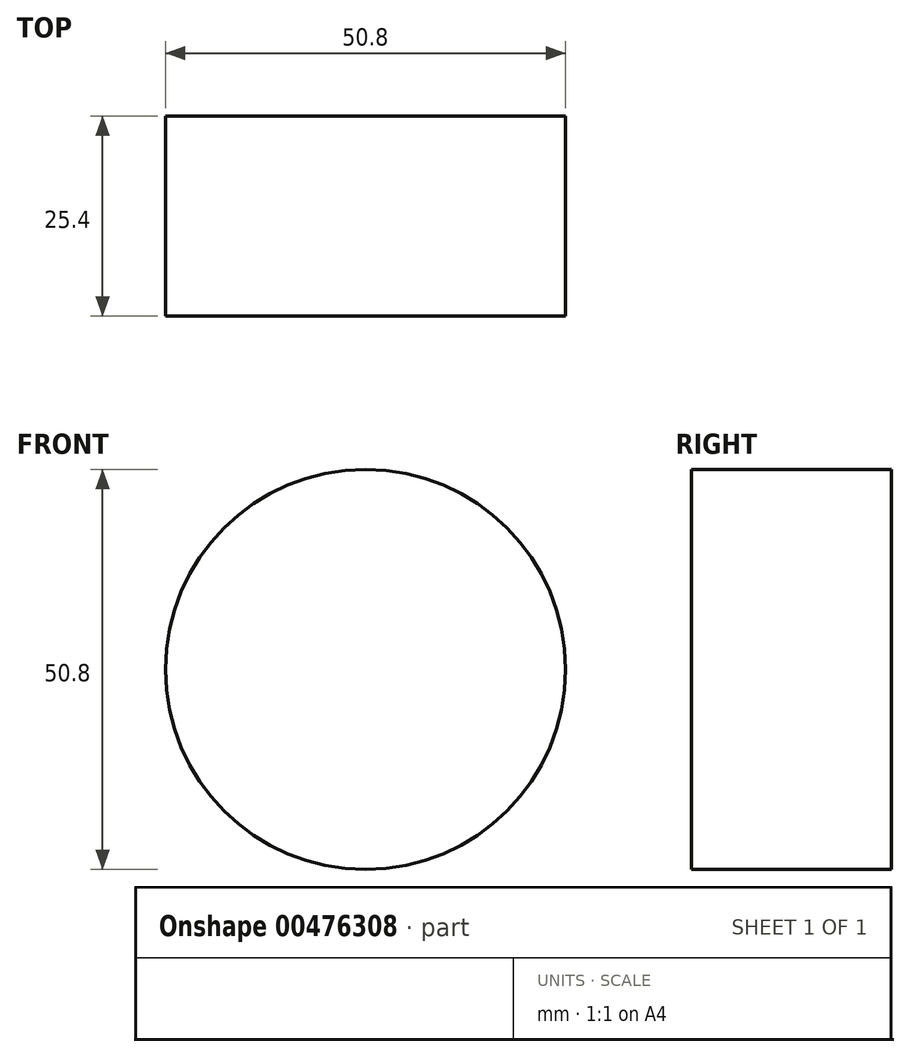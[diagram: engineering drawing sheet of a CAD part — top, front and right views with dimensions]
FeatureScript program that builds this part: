
annotation { "Feature Type Name" : "Feature", "Feature Type Description" : "" }
export const myFeature = defineFeature(function(context is Context, id is Id, definition is map)
    precondition{}
    {
        {
            var Q0;
            Q0=qCreatedBy(makeId("Front.planeOp"),FACE);
            var sketch = newSketch(context, id + "F0", { "sketchPlane" : qUnion([Q0])});
            skCircle(sketch, "E0", {"center": v(0, 0) * mm, "radius": 25.4 * mm});
            skLineSegment(sketch, "E1", {"start": v(-152.4, -31.75) * mm, "end": v(50.8, -31.75) * mm});
            skCircle(sketch, "E2", {"center": v(-161.93, -57.15) * mm, "radius": 19.05 * mm});
            skCircle(sketch, "E3", {"center": v(-6.35, -57.15) * mm, "radius": 19.05 * mm});
            skLineSegment(sketch, "E4", {"start": v(-25.4, 0) * mm, "end": v(-25.4, -57.15) * mm, "construction": true});
            skSolve(sketch);
        }
        {
            var Q0;
            Q0=makeQuery(id+"F0.imprint","IMPRINT",FACE,{"disambiguationData":[TD([[makeQuery(id+"F0.imprint","IMPRINT",EDGE,{"derivedFrom":sQuery(id+"F0.wireOp",EDGE,"E0")}),1.0]])]});
            extrude(context, id + "F1", {"entities" : qUnion([Q0]), "depth" : 25.4 * mm});
        }
    });
